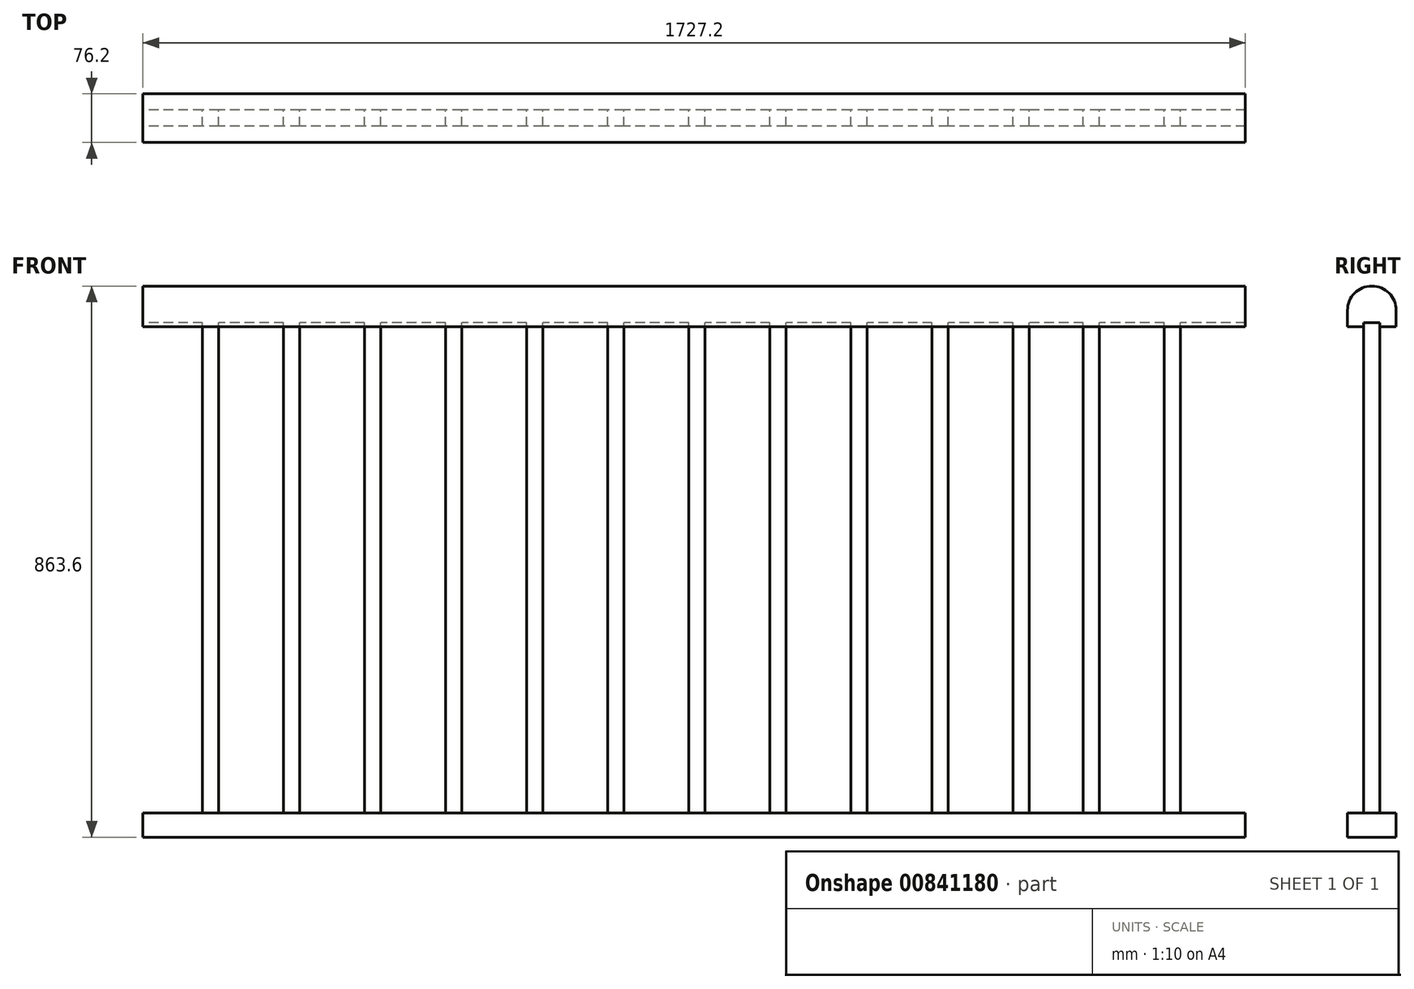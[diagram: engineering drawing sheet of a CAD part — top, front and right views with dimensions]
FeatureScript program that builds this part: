
annotation { "Feature Type Name" : "Feature", "Feature Type Description" : "" }
export const myFeature = defineFeature(function(context is Context, id is Id, definition is map)
    precondition{}
    {
        {
            var Q0;
            Q0=qCreatedBy(makeId("Right.planeOp"),FACE);
            var sketch = newSketch(context, id + "F0", { "sketchPlane" : qUnion([Q0])});
            skLineSegment(sketch, "E0.top", {"start": v(0, -25.4) * mm, "end": v(25.4, -25.4) * mm});
            skLineSegment(sketch, "E0.left", {"start": v(0, 0) * mm, "end": v(0, -25.4) * mm});
            skLineSegment(sketch, "E0.right", {"start": v(76.2, 0) * mm, "end": v(76.2, -25.4) * mm});
            skArc(sketch, "E1", {"start": v(76.2, 0) * mm, "mid": v(38.1, 38.1) * mm, "end": v(0, 0) * mm});
            skLineSegment(sketch, "E2", {"start": v(50.8, -25.4) * mm, "end": v(50.8, -19.05) * mm});
            skLineSegment(sketch, "E3", {"start": v(50.8, -19.05) * mm, "end": v(25.4, -19.05) * mm});
            skLineSegment(sketch, "E4", {"start": v(25.4, -19.05) * mm, "end": v(25.4, -25.4) * mm});
            skLineSegment(sketch, "E5.trimOffspring", {"start": v(50.8, -25.4) * mm, "end": v(76.2, -25.4) * mm});
            skLineSegment(sketch, "E6.bottom", {"start": v(0, -787.4) * mm, "end": v(76.2, -787.4) * mm});
            skLineSegment(sketch, "E6.top", {"start": v(0, -825.5) * mm, "end": v(76.2, -825.5) * mm});
            skLineSegment(sketch, "E6.left", {"start": v(0, -787.4) * mm, "end": v(0, -825.5) * mm});
            skLineSegment(sketch, "E6.right", {"start": v(76.2, -787.4) * mm, "end": v(76.2, -825.5) * mm});
            skSolve(sketch);
        }
        {
            var Q0;
            Q0=makeQuery(id+"F0.imprint","IMPRINT",FACE,{"disambiguationData":[TD([[makeQuery(id+"F0.imprint","IMPRINT",EDGE,{"derivedFrom":sQuery(id+"F0.wireOp",EDGE,"E0.top")}),1.0]])]});
            var Q1;
            Q1=makeQuery(id+"F0.imprint","IMPRINT",FACE,{"disambiguationData":[TD([[makeQuery(id+"F0.imprint","IMPRINT",EDGE,{"derivedFrom":sQuery(id+"F0.wireOp",EDGE,"E6.bottom")}),-1.0]])]});
            extrude(context, id + "F1", {"entities" : qUnion([Q0, Q1]), "depth" : 1727.2 * mm, "offsetDistance" : 25.4 * mm});
        }
        {
            var Q0;
            Q0=makeQuery(id+"F1.opExtrude","SWEPT_FACE",FACE,{"disambiguationData":[OSD([sQuery(id+"F0.wireOp",EDGE,"E3")])]});
            var sketch = newSketch(context, id + "F2", { "sketchPlane" : qUnion([Q0])});
            skLineSegment(sketch, "E7.bottom", {"start": v(1625.6, -25.4) * mm, "end": v(1600.2, -25.4) * mm});
            skLineSegment(sketch, "E7.top", {"start": v(1625.6, -50.8) * mm, "end": v(1600.2, -50.8) * mm});
            skLineSegment(sketch, "E7.right", {"start": v(1625.6, -25.4) * mm, "end": v(1625.6, -50.8) * mm});
            skLineSegment(sketch, "E8", {"start": v(1600.2, -25.4) * mm, "end": v(1600.2, -50.8) * mm});
            skLineSegment(sketch, "E9.bottom", {"start": v(1473.2, -25.4) * mm, "end": v(1498.6, -25.4) * mm});
            skLineSegment(sketch, "E9.top", {"start": v(1473.2, -50.8) * mm, "end": v(1498.6, -50.8) * mm});
            skLineSegment(sketch, "E9.left", {"start": v(1473.2, -25.4) * mm, "end": v(1473.2, -50.8) * mm});
            skLineSegment(sketch, "E9.right", {"start": v(1498.6, -25.4) * mm, "end": v(1498.6, -50.8) * mm});
            skLineSegment(sketch, "E10.bottom", {"start": v(1363.48, -25.4) * mm, "end": v(1388.88, -25.4) * mm});
            skLineSegment(sketch, "E10.top", {"start": v(1363.48, -50.8) * mm, "end": v(1388.88, -50.8) * mm});
            skLineSegment(sketch, "E10.left", {"start": v(1363.48, -25.4) * mm, "end": v(1363.48, -50.8) * mm});
            skLineSegment(sketch, "E10.right", {"start": v(1388.88, -25.4) * mm, "end": v(1388.88, -50.8) * mm});
            skLineSegment(sketch, "E11.bottom", {"start": v(1236.48, -25.4) * mm, "end": v(1261.88, -25.4) * mm});
            skLineSegment(sketch, "E11.top", {"start": v(1236.48, -50.8) * mm, "end": v(1261.88, -50.8) * mm});
            skLineSegment(sketch, "E11.left", {"start": v(1236.48, -25.4) * mm, "end": v(1236.48, -50.8) * mm});
            skLineSegment(sketch, "E11.right", {"start": v(1261.88, -25.4) * mm, "end": v(1261.88, -50.8) * mm});
            skLineSegment(sketch, "E12.bottom", {"start": v(1109.48, -25.4) * mm, "end": v(1134.88, -25.4) * mm});
            skLineSegment(sketch, "E12.top", {"start": v(1109.48, -50.8) * mm, "end": v(1134.88, -50.8) * mm});
            skLineSegment(sketch, "E12.left", {"start": v(1109.48, -25.4) * mm, "end": v(1109.48, -50.8) * mm});
            skLineSegment(sketch, "E12.right", {"start": v(1134.88, -25.4) * mm, "end": v(1134.88, -50.8) * mm});
            skLineSegment(sketch, "E13.bottom", {"start": v(855.48, -25.4) * mm, "end": v(880.88, -25.4) * mm});
            skLineSegment(sketch, "E13.top", {"start": v(855.48, -50.8) * mm, "end": v(880.88, -50.8) * mm});
            skLineSegment(sketch, "E13.left", {"start": v(855.48, -25.4) * mm, "end": v(855.48, -50.8) * mm});
            skLineSegment(sketch, "E13.right", {"start": v(880.88, -25.4) * mm, "end": v(880.88, -50.8) * mm});
            skLineSegment(sketch, "E14.bottom", {"start": v(982.48, -25.4) * mm, "end": v(1007.88, -25.4) * mm});
            skLineSegment(sketch, "E14.top", {"start": v(982.48, -50.8) * mm, "end": v(1007.88, -50.8) * mm});
            skLineSegment(sketch, "E14.left", {"start": v(982.48, -25.4) * mm, "end": v(982.48, -50.8) * mm});
            skLineSegment(sketch, "E14.right", {"start": v(1007.88, -25.4) * mm, "end": v(1007.88, -50.8) * mm});
            skLineSegment(sketch, "E15.bottom", {"start": v(728.48, -25.4) * mm, "end": v(753.88, -25.4) * mm});
            skLineSegment(sketch, "E15.top", {"start": v(728.48, -50.8) * mm, "end": v(753.88, -50.8) * mm});
            skLineSegment(sketch, "E15.left", {"start": v(728.48, -25.4) * mm, "end": v(728.48, -50.8) * mm});
            skLineSegment(sketch, "E15.right", {"start": v(753.88, -25.4) * mm, "end": v(753.88, -50.8) * mm});
            skLineSegment(sketch, "E16.bottom", {"start": v(601.48, -25.4) * mm, "end": v(626.88, -25.4) * mm});
            skLineSegment(sketch, "E16.top", {"start": v(601.48, -50.8) * mm, "end": v(626.88, -50.8) * mm});
            skLineSegment(sketch, "E16.left", {"start": v(601.48, -25.4) * mm, "end": v(601.48, -50.8) * mm});
            skLineSegment(sketch, "E16.right", {"start": v(626.88, -25.4) * mm, "end": v(626.88, -50.8) * mm});
            skLineSegment(sketch, "E17.bottom", {"start": v(474.48, -25.4) * mm, "end": v(499.88, -25.4) * mm});
            skLineSegment(sketch, "E17.top", {"start": v(474.48, -50.8) * mm, "end": v(499.88, -50.8) * mm});
            skLineSegment(sketch, "E17.left", {"start": v(474.48, -25.4) * mm, "end": v(474.48, -50.8) * mm});
            skLineSegment(sketch, "E17.right", {"start": v(499.88, -25.4) * mm, "end": v(499.88, -50.8) * mm});
            skLineSegment(sketch, "E18.bottom", {"start": v(347.48, -25.4) * mm, "end": v(372.88, -25.4) * mm});
            skLineSegment(sketch, "E18.top", {"start": v(347.48, -50.8) * mm, "end": v(372.88, -50.8) * mm});
            skLineSegment(sketch, "E18.left", {"start": v(347.48, -25.4) * mm, "end": v(347.48, -50.8) * mm});
            skLineSegment(sketch, "E18.right", {"start": v(372.88, -25.4) * mm, "end": v(372.88, -50.8) * mm});
            skLineSegment(sketch, "E19.bottom", {"start": v(220.48, -25.4) * mm, "end": v(245.88, -25.4) * mm});
            skLineSegment(sketch, "E19.top", {"start": v(220.48, -50.8) * mm, "end": v(245.88, -50.8) * mm});
            skLineSegment(sketch, "E19.left", {"start": v(220.48, -25.4) * mm, "end": v(220.48, -50.8) * mm});
            skLineSegment(sketch, "E19.right", {"start": v(245.88, -25.4) * mm, "end": v(245.88, -50.8) * mm});
            skLineSegment(sketch, "E20.bottom", {"start": v(93.48, -25.4) * mm, "end": v(118.88, -25.4) * mm});
            skLineSegment(sketch, "E20.top", {"start": v(93.48, -50.8) * mm, "end": v(118.88, -50.8) * mm});
            skLineSegment(sketch, "E20.left", {"start": v(93.48, -25.4) * mm, "end": v(93.48, -50.8) * mm});
            skLineSegment(sketch, "E20.right", {"start": v(118.88, -25.4) * mm, "end": v(118.88, -50.8) * mm});
            skSolve(sketch);
        }
        {
            var Q0;
            Q0 = qSketchRegion(id + "F2", true);
            var Q1;
            Q1=makeQuery(id+"F1.opExtrude","SWEPT_FACE",FACE,{"disambiguationData":[OSD([sQuery(id+"F0.wireOp",EDGE,"E6.bottom")])]});
            extrude(context, id + "F3", {"entities" : qUnion([Q0, Q1]), "operationType" : NewBodyOperationType.ADD, "endBound" : BoundingType.UP_TO_NEXT, "depth" : 25.4 * mm, "offsetDistance" : 25.4 * mm});
        }
    });
